# Revit family: Roof-Ladder
name_source: partatom
category: Generic Models
units: mm (PartAtom-declared; Revit-internal decimal feet)

## family parameters
Always vertical = Yes
Can host rebar = No
Classification Number = 23.30.70.17
Cut with Voids When Loaded = No
Maintain Annotation Orientation = No
Part Type = Normal
Room Calculation Point = No
Round Connector Dimension = Use Diameter
Shared = No
Work Plane-Based = No

## types (1)
- As Specified in 05 51 13
    Assembly Code = E1090900
    Building Code Conformance = ANSI A14.3
    Construction Details = http://www.arcat.com
    Default Elevation = 0' - 0"
    Description = Roof Access Ladder as Specified in 05 51 13
    Expected Lifespan (Years) = 0
    Green Building-LEED = http://www.arcat.com
    Height = 12' - 0"
    Keynote = 05 51 33
    Maintenance Schedule (Months) = 0
    Manufacturer = Generic
    Manufacturer Fax = (203) 939-2444
    Manufacturer Website = http://www.arcat.com
    Model = Generic
    Product Data = http://www.arcat.com
    Product Properties = http://www.arcat.com
    Specification = http://www.arcat.com
    Step Height = 1' - 3"
    Warranty Duration (Years) = 0
    hand rail = 3
    rail = 3' - 7 31/32"
    step = 10

## geometry (parser evidence)
native form markers: Blend x6, Sweep x4
no freeform markers — native parametric forms only
